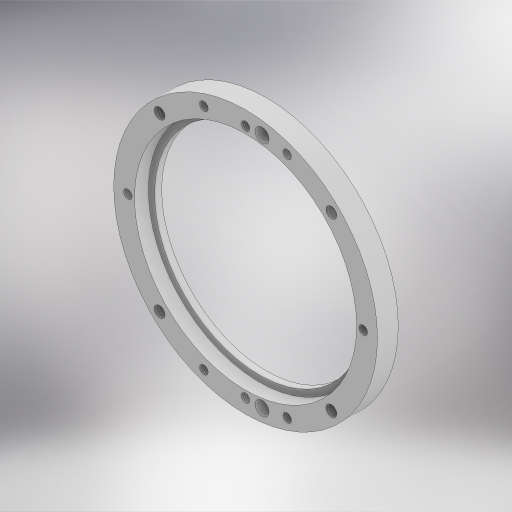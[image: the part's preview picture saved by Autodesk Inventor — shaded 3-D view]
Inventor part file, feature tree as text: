
AUTODESK INVENTOR PART (.ipt)
format: ipt  version: 2023.4 (Build 274418000, 418)  size: 400,896 bytes
history: native  units: in
note: dims shown in document units (in); Inventor stores cm internally (conversion verified against a paired STEP export)
features: sketch x7, hole x4, extrude x3, projected_geometry x1
ambient origin geometry x8: Origin, YZ Plane, XZ Plane, XY Plane, X Axis, Y Axis, Z Axis, Center Point
bodies: Solid1 (feature_tree)
feature tree (15):
  extrude  "Extrusion1"  Depth=0.5in
  extrude  "Extrusion2"  Depth=0.375in
  hole  "Hole1"  [1 undecoded]
  extrude  "Extrusion3"  Depth=0.25in
  hole  "Hole2"  [1 undecoded]
  hole  "Hole3"  [1 undecoded]
  hole  "Hole4"  [1 undecoded]
  sketch  "Sketch1"  dims[d0=4.75in d1=0.5in]
  sketch  "Sketch2"  dims[d2=0.375in d3=0.0in d4=4.0in]
  sketch  "Sketch3"  dims[d5=0.25in d6=0.0in d7=2.12in]
  sketch  "Sketch4"  dims[d8=1.5748in d10=360.0deg]
  sketch  "Sketch5"  dims[d12=0.156in d13=0.38in d14=0.375in d15=0.25in d16=0.5635in d17=0.536in d18=0.8108in d19=3.775in]
  sketch  "Sketch6"  dims[d20=0.25in d21=0.0in d22=4.375in]
  sketch  "Sketch7"  dims[d25=0.75in d26=0.75in d27=0.156in d28=0.38in d29=0.119in d30=0.25in d31=0.5635in d32=1.0in d33=0.8108in d34=4.375in d35=45.0deg d36=1.5748in d38=360.0deg d40=0.196in d41=0.5in d42=0.375in d43=0.25in d44=0.5635in d45=1.0in d46=0.8108in d47=4.11in d49=4.3in d50=0.055in d51=0.25in d52=0.75in d53=0.375in d54=0.25in d55=0.5635in d56=1.0in d57=0.8108in]
  projected_geometry  "Projected Loop1"
note: 4 required parameter values undecoded (feature->parameter linkage not recoverable at this tier; creation-order binding heuristic only, values carry confidence <= 0.55)
